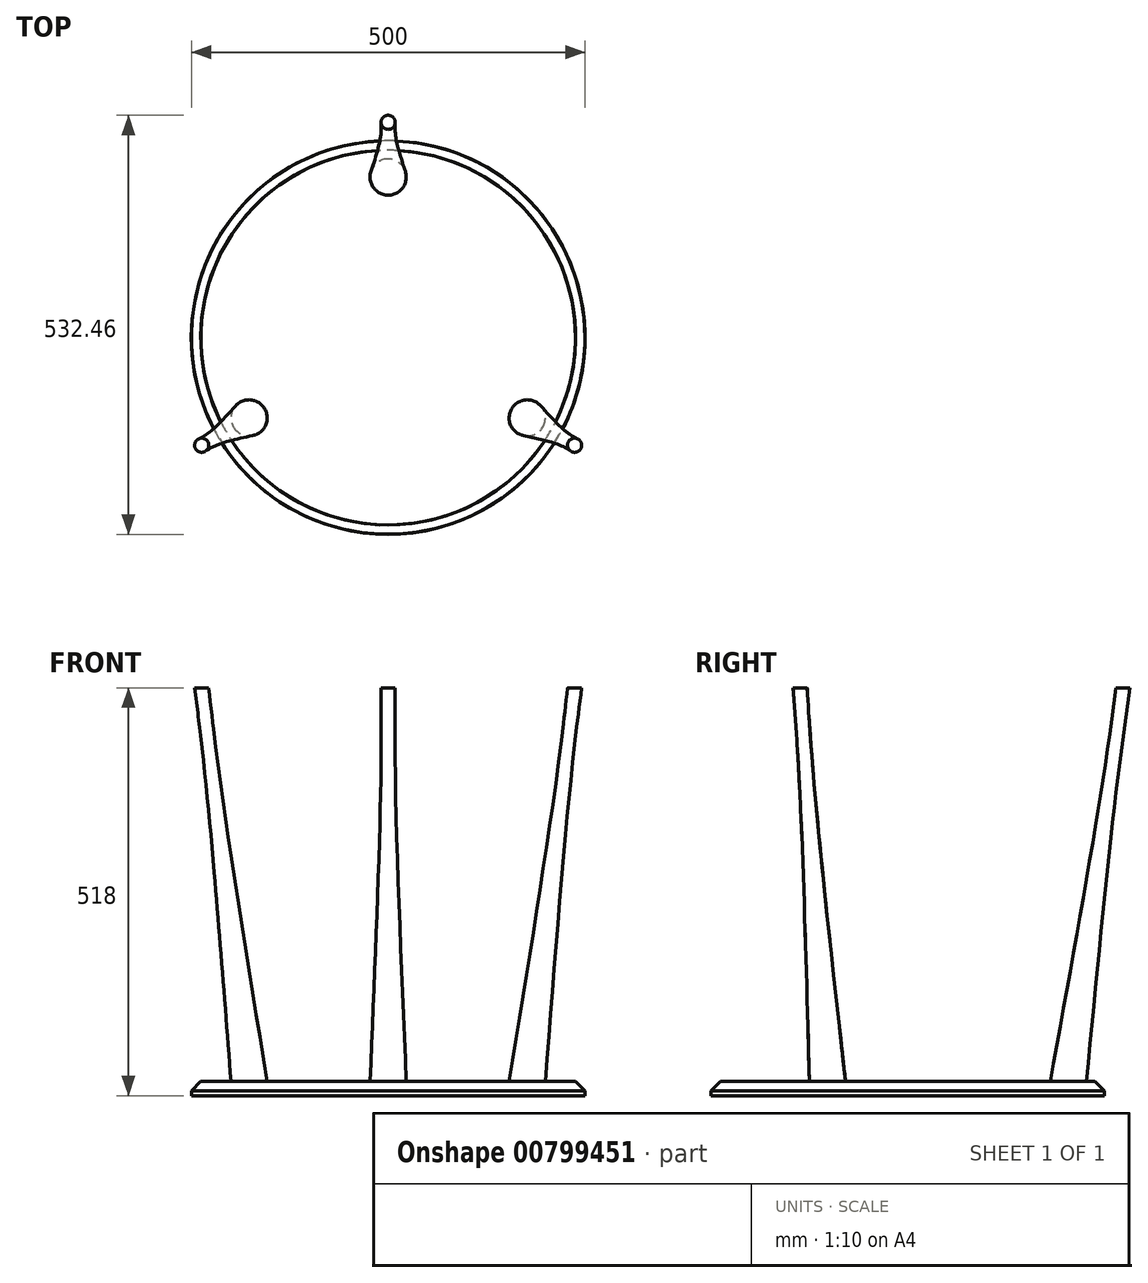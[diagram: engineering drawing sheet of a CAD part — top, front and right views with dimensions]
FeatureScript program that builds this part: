
annotation { "Feature Type Name" : "Feature", "Feature Type Description" : "" }
export const myFeature = defineFeature(function(context is Context, id is Id, definition is map)
    precondition{}
    {
        {
            var Q0;
            Q0=qCreatedBy(makeId("Top.planeOp"),FACE);
            var sketch = newSketch(context, id + "F0", { "sketchPlane" : qUnion([Q0])});
            skCircle(sketch, "E0", {"center": v(0, 0) * mm, "radius": 250 * mm});
            skCircle(sketch, "E1", {"center": v(0, 0) * mm, "radius": 204 * mm, "construction": true});
            skLineSegment(sketch, "E2", {"start": v(0, 0) * mm, "end": v(0, 228.58) * mm, "construction": true});
            skLineSegment(sketch, "E3", {"start": v(0, 0) * mm, "end": v(249.69, -144.16) * mm, "construction": true});
            skLineSegment(sketch, "E4", {"start": v(0, 0) * mm, "end": v(-215.96, -124.68) * mm, "construction": true});
            skCircle(sketch, "E5", {"center": v(0, 204) * mm, "radius": 9 * mm, "construction": true});
            skCircle(sketch, "E6", {"center": v(176.67, -102) * mm, "radius": 9 * mm, "construction": true});
            skCircle(sketch, "E7", {"center": v(-176.67, -102) * mm, "radius": 9 * mm, "construction": true});
            skSolve(sketch);
        }
        {
            var Q0;
            Q0=makeQuery(id+"F0.imprint","IMPRINT",FACE,{"disambiguationData":[TD([[makeQuery(id+"F0.imprint","IMPRINT",EDGE,{"derivedFrom":sQuery(id+"F0.wireOp",EDGE,"E0")}),1.0]])]});
            cPlane(context, id + "F1", {"entities" : qUnion([Q0]), "cplaneType" : CPlaneType.OFFSET, "offset" : 18 * mm, "oppositeDirection" : true, "width" : 150 * mm, "height" : 150 * mm});
        }
        {
            var Q0;
            Q0=qCreatedBy(id+"F1.planeOp",FACE);
            var sketch = newSketch(context, id + "F2", { "sketchPlane" : qUnion([Q0])});
            skCircle(sketch, "E8", {"center": v(0, 0) * mm, "radius": 200.83 * mm, "construction": true});
            skLineSegment(sketch, "E9", {"start": v(0, 0) * mm, "end": v(0, 172.1) * mm, "construction": true});
            skLineSegment(sketch, "E10", {"start": v(0, 0) * mm, "end": v(213.99, -123.55) * mm, "construction": true});
            skLineSegment(sketch, "E11", {"start": v(0, 0) * mm, "end": v(-195.16, -112.67) * mm, "construction": true});
            skCircle(sketch, "E12", {"center": v(-173.92, -100.41) * mm, "radius": 9 * mm});
            skCircle(sketch, "E13", {"center": v(173.92, -100.41) * mm, "radius": 9 * mm});
            skCircle(sketch, "E14", {"center": v(0, 200.83) * mm, "radius": 9 * mm});
            skSolve(sketch);
        }
        {
            var Q0;
            Q0=makeQuery(id+"F0.imprint","IMPRINT",FACE,{"disambiguationData":[TD([[makeQuery(id+"F0.imprint","IMPRINT",EDGE,{"derivedFrom":sQuery(id+"F0.wireOp",EDGE,"E0")}),1.0]])]});
            extrude(context, id + "F3", {"entities" : qUnion([Q0]), "oppositeDirection" : true, "depth" : 18 * mm});
        }
        {
            var Q0;
            Q0=qCreatedBy(makeId("Right.planeOp"),FACE);
            var sketch = newSketch(context, id + "F4", { "sketchPlane" : qUnion([Q0])});
            skLineSegment(sketch, "E15", {"start": v(204, 0) * mm, "end": v(200.83, -18) * mm, "construction": true});
            skLineSegment(sketch, "E16", {"start": v(204, 0) * mm, "end": v(273.46, 393.92) * mm});
            skSolve(sketch);
        }
        {
            var Q0;
            Q0=makeQuery(id+"F3.opExtrude","CAP_EDGE",EDGE,{"disambiguationData":[OSD([sQuery(id+"F0.wireOp",EDGE,"E0")])],"isStart":true});
            chamfer(context, id + "F5", {"entities" : qUnion([Q0]), "width" : 12 * mm, "tangentPropagation" : true});
        }
        {
            var Q0;
            Q0=makeQuery(id+"F0.imprint","IMPRINT",FACE,{"disambiguationData":[TD([[makeQuery(id+"F0.imprint","IMPRINT",EDGE,{"derivedFrom":sQuery(id+"F0.wireOp",EDGE,"E0")}),1.0]])]});
            var sketch = newSketch(context, id + "F6", { "sketchPlane" : qUnion([Q0])});
            skCircle(sketch, "E17.0", {"center": v(0, 204) * mm, "radius": 23 * mm});
            skSolve(sketch);
        }
        {
            var Q0;
            Q0=makeQuery(id+"F6.imprint","IMPRINT",FACE,{"disambiguationData":[TD([[makeQuery(id+"F6.imprint","IMPRINT",EDGE,{"derivedFrom":sQuery(id+"F6.wireOp",EDGE,"E17.0")}),-1.0]])]});
            cPlane(context, id + "F7", {"entities" : qUnion([Q0]), "cplaneType" : CPlaneType.OFFSET, "offset" : 500 * mm, "width" : 150 * mm, "height" : 150 * mm});
        }
        {
            var Q0;
            Q0=qCreatedBy(id+"F7.planeOp",FACE);
            var sketch = newSketch(context, id + "F8", { "sketchPlane" : qUnion([Q0])});
            skCircle(sketch, "E18", {"center": v(0, 273.46) * mm, "radius": 9 * mm});
            skSolve(sketch);
        }
        {
            var Q1;
            Q1=makeQuery(id+"F8.imprint","IMPRINT",FACE,{"disambiguationData":[TD([[makeQuery(id+"F8.imprint","IMPRINT",EDGE,{"derivedFrom":sQuery(id+"F8.wireOp",EDGE,"E18")}),1.0]])]});
            var Q2;
            Q2=makeQuery(id+"F6.imprint","IMPRINT",FACE,{"disambiguationData":[TD([[makeQuery(id+"F6.imprint","IMPRINT",EDGE,{"derivedFrom":sQuery(id+"F6.wireOp",EDGE,"E17.0")}),1.0]])]});
            loft(context, id + "F9", {"operationType" : NewBodyOperationType.ADD, "sheetProfilesArray" : [{ "sheetProfileEntities" : qUnion([Q1]) }, { "sheetProfileEntities" : qUnion([Q2]) }]});
        }
        {
            var Q0;
            Q0=makeQuery(id+"F2.imprint","IMPRINT",FACE,{"disambiguationData":[TD([[makeQuery(id+"F2.imprint","IMPRINT",EDGE,{"derivedFrom":sQuery(id+"F2.wireOp",EDGE,"E14")}),1.0]])]});
            var Q1;
            Q1=makeQuery(id+"F2.imprint","IMPRINT",FACE,{"disambiguationData":[TD([[makeQuery(id+"F2.imprint","IMPRINT",EDGE,{"derivedFrom":sQuery(id+"F2.wireOp",EDGE,"E12")}),1.0]])]});
            var Q2;
            Q2=makeQuery(id+"F2.imprint","IMPRINT",FACE,{"disambiguationData":[TD([[makeQuery(id+"F2.imprint","IMPRINT",EDGE,{"derivedFrom":sQuery(id+"F2.wireOp",EDGE,"E13")}),1.0]])]});
            extrude(context, id + "F10", {"entities" : qUnion([Q0, Q1, Q2]), "operationType" : NewBodyOperationType.ADD, "depth" : 1 * mm});
        }
        {
            var Q0;
            Q0=qCreatedBy(makeId("Front.planeOp"),FACE);
            var sketch = newSketch(context, id + "F11", { "sketchPlane" : qUnion([Q0])});
            skLineSegment(sketch, "E19", {"start": v(0, 0) * mm, "end": v(0, -114.72) * mm});
            skSolve(sketch);
        }
        {
            var Q0;
            Q0=makeQuery(id+"F3.opExtrude","SWEPT_BODY",BODY,{"disambiguationData":[OSD([sQuery(id+"F0.wireOp",EDGE,"E0")])]});
            var Q1;
            Q1=sQuery(id+"F11.wireOp",EDGE,"E19");
            transform(context, id + "F12", {"entities" : qUnion([Q0]), "transformType" : TransformType.ROTATION, "transformAxis" : qUnion([Q1]), "angle" : 120 * degree, "makeCopy" : true});
        }
        {
            var Q0;
            Q0=makeQuery(id+"F3.opExtrude","SWEPT_BODY",BODY,{"disambiguationData":[OSD([sQuery(id+"F0.wireOp",EDGE,"E0")])]});
            var Q1;
            Q1=sQuery(id+"F11.wireOp",EDGE,"E19");
            transform(context, id + "F13", {"entities" : qUnion([Q0]), "transformType" : TransformType.ROTATION, "transformAxis" : qUnion([Q1]), "angle" : 240 * degree, "makeCopy" : true});
        }
    });
